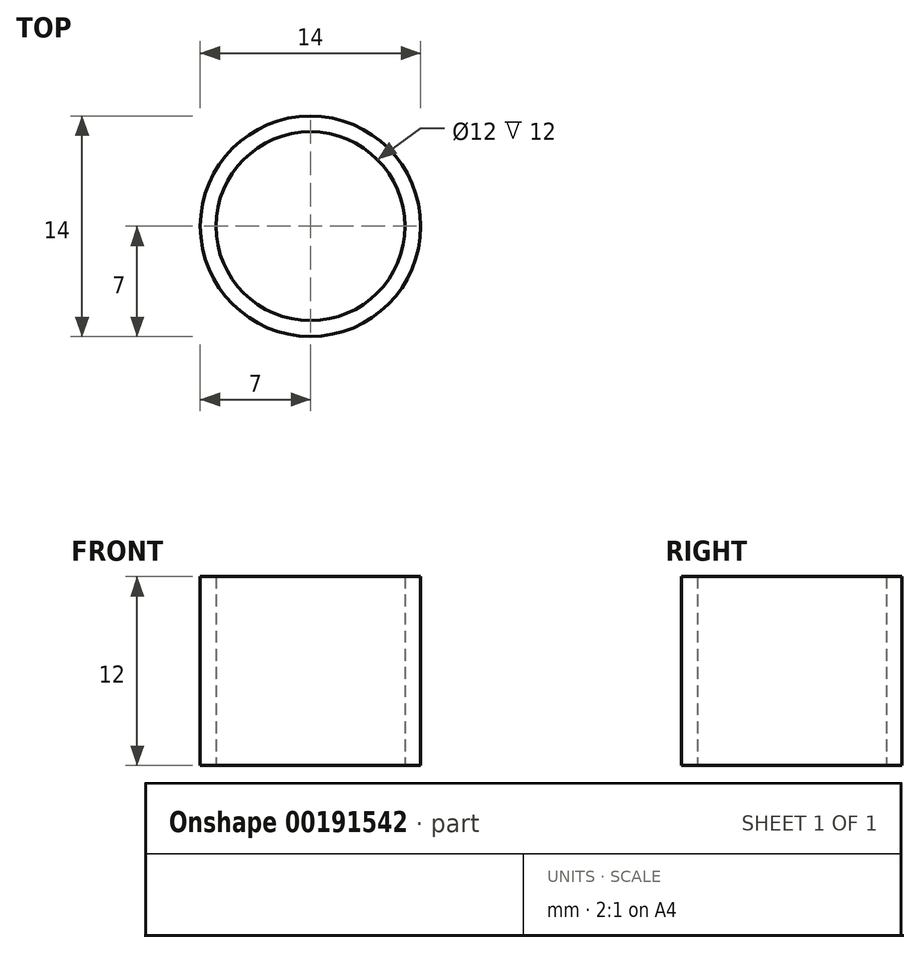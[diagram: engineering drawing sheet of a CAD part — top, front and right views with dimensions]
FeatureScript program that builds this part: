
annotation { "Feature Type Name" : "Feature", "Feature Type Description" : "" }
export const myFeature = defineFeature(function(context is Context, id is Id, definition is map)
    precondition{}
    {
        {
            var Q0;
            Q0=qCreatedBy(makeId("Top.planeOp"),FACE);
            var sketch = newSketch(context, id + "F0", { "sketchPlane" : qUnion([Q0])});
            skCircle(sketch, "E0", {"center": v(0, 0) * mm, "radius": 6 * mm});
            skCircle(sketch, "E1", {"center": v(0, 0) * mm, "radius": 7 * mm});
            skSolve(sketch);
        }
        {
            var Q0;
            Q0 = qSketchRegion(id + "F0", true);
            extrude(context, id + "F1", {"entities" : qUnion([Q0]), "depth" : 12 * mm});
        }
    });
